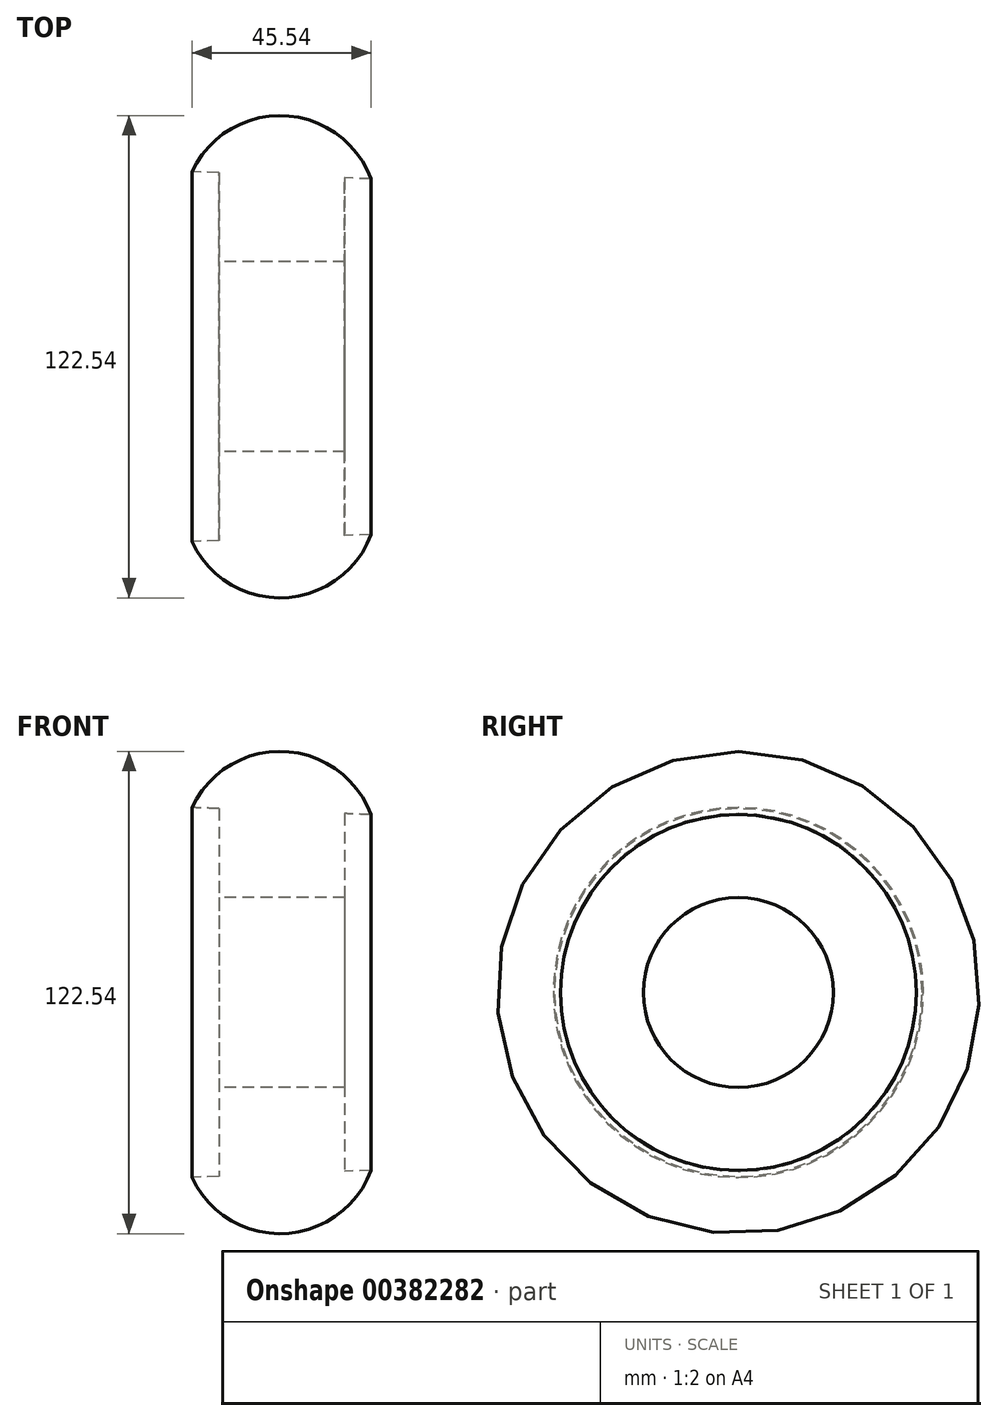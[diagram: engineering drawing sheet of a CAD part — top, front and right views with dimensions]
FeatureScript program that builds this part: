
annotation { "Feature Type Name" : "Feature", "Feature Type Description" : "" }
export const myFeature = defineFeature(function(context is Context, id is Id, definition is map)
    precondition{}
    {
        {
            var Q0;
            Q0=qCreatedBy(makeId("Front.planeOp"),FACE);
            var sketch = newSketch(context, id + "F0", { "sketchPlane" : qUnion([Q0])});
            skLineSegment(sketch, "E0", {"start": v(-70.58, 0) * mm, "end": v(69.86, 0) * mm, "construction": true});
            skArc(sketch, "E1", {"start": v(23.77, 45.18) * mm, "mid": v(1.6, 61.25) * mm, "end": v(-21.77, 47) * mm});
            skLineSegment(sketch, "E2", {"start": v(-21.77, 47) * mm, "end": v(23.77, 45.18) * mm});
            skLineSegment(sketch, "E3.bottom", {"start": v(-14.87, 46.72) * mm, "end": v(17.06, 46.72) * mm});
            skLineSegment(sketch, "E3.top", {"start": v(-14.87, 24.13) * mm, "end": v(17.06, 24.13) * mm});
            skLineSegment(sketch, "E3.left", {"start": v(-14.87, 46.72) * mm, "end": v(-14.87, 24.13) * mm});
            skLineSegment(sketch, "E3.right", {"start": v(17.06, 46.72) * mm, "end": v(17.06, 24.13) * mm});
            skSolve(sketch);
        }
        {
            var Q0;
            Q0 = qSketchRegion(id + "F0", true);
            var Q1;
            Q1=sQuery(id+"F0.wireOp",EDGE,"E0");
            revolve(context, id + "F1", {"entities" : qUnion([Q0]), "axis" : qUnion([Q1]), "revolveType" : RevolveType.FULL});
        }
    });
